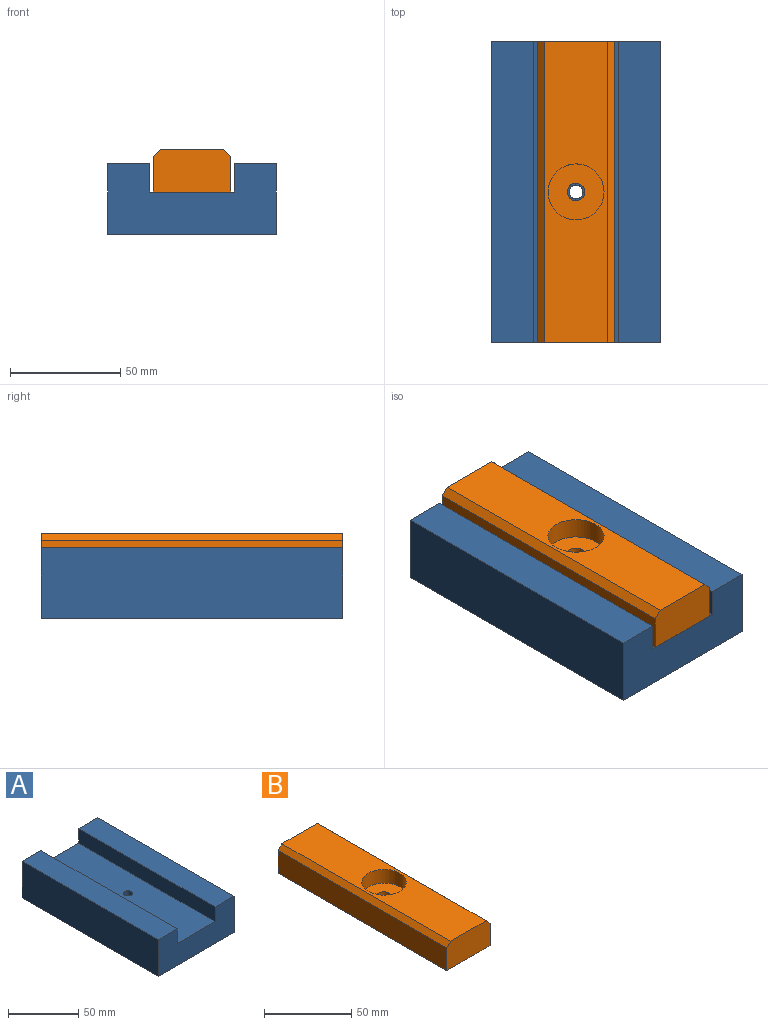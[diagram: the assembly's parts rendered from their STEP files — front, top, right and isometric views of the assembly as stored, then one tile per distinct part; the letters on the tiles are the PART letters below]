
ASSEMBLY  parts=2 mates=1
PART A: 13 faces, bbox 76.2x136.5x31.8 mm
  f0: plane 136.53x19.05mm, normal (0,0,1), area 2600.8mm2, adj f1,f2,f3,f7
  f1: plane 76.2x31.75mm, normal (0,-1,0), area 1935.5mm2, adj f0,f2,f4,f5,f6,f7,f8,f9
  f2: plane 136.53x31.75mm, normal (1,0,0), area 4334.7mm2, adj f0,f1,f3,f6
  f3: plane 76.2x31.75mm, normal (0,1,0), area 1935.5mm2, adj f0,f2,f4,f5,f6,f7,f8,f9
  f4: plane 136.53x31.75mm, normal (-1,0,0), area 4334.7mm2, adj f1,f3,f5,f6
  f5: plane 136.53x19.05mm, normal (0,0,1), area 2600.8mm2, adj f1,f3,f4,f8
  f6: plane 136.53x76.2mm, normal (0,0,-1), area 10118.2mm2, adj f1,f2,f3,f4,f10
  f7: plane 136.53x12.7mm, normal (-1,0,0), area 1733.9mm2, adj f0,f1,f3,f9
  f8: plane 136.53x12.7mm, normal (1,0,0), area 1733.9mm2, adj f1,f3,f5,f9
  f9: plane 136.53x38.1mm, normal (0,0,1), area 5169.9mm2, adj f1,f3,f7,f8,f12
  f10: cylinder r=9.53mm len=19.05mm, axis (0,0,-1), area 760.1mm2, adj f6,f11
  f11: plane 19.05x19.05mm, normal (0,0,-1), area 253.4mm2, adj f10,f12
  f12: cylinder r=3.17mm len=6.35mm, axis (0,0,1), area 126.7mm2, adj f9,f11
PART B: 11 faces, bbox 34.9x136.5x19.1 mm
  f0: plane 136.53x15.88mm, normal (-1,0,0), area 2167.3mm2, adj f1,f4,f5,f6
  f1: plane 136.53x34.93mm, normal (0,0,-1), area 4718.7mm2, adj f0,f2,f4,f5,f10
  f2: plane 136.53x15.88mm, normal (1,0,0), area 2167.3mm2, adj f1,f4,f5,f7
  f3: plane 136.53x28.58mm, normal (0,0,1), area 3394.5mm2, adj f4,f5,f6,f7,f8
  f4: plane 34.93x19.05mm, normal (0,-1,0), area 655.2mm2, adj f0,f1,f2,f3,f6,f7
  f5: plane 34.93x19.05mm, normal (0,1,0), area 655.2mm2, adj f0,f1,f2,f3,f6,f7
  f6: plane 136.53x3.18mm, normal (-0.71,0,0.71), area 613mm2, adj f0,f3,f4,f5
  f7: plane 136.53x3.18mm, normal (0.71,0,0.71), area 613mm2, adj f2,f3,f4,f5
  f8: cylinder r=12.7mm len=25.4mm, axis (0,0,1), area 760.1mm2, adj f3,f9
  f9: plane 25.4x25.4mm, normal (0,0,1), area 457.2mm2, adj f8,f10
  f10: cylinder r=3.97mm len=9.53mm, axis (0,0,1), area 237.5mm2, adj f1,f9
PLACE A at identity
PLACE B t=(-17.46,68.26,38.1)mm
MATE fastened B.f8 <-> A.f10  axis (0,0,-1) through (0,0,19.05)mm
